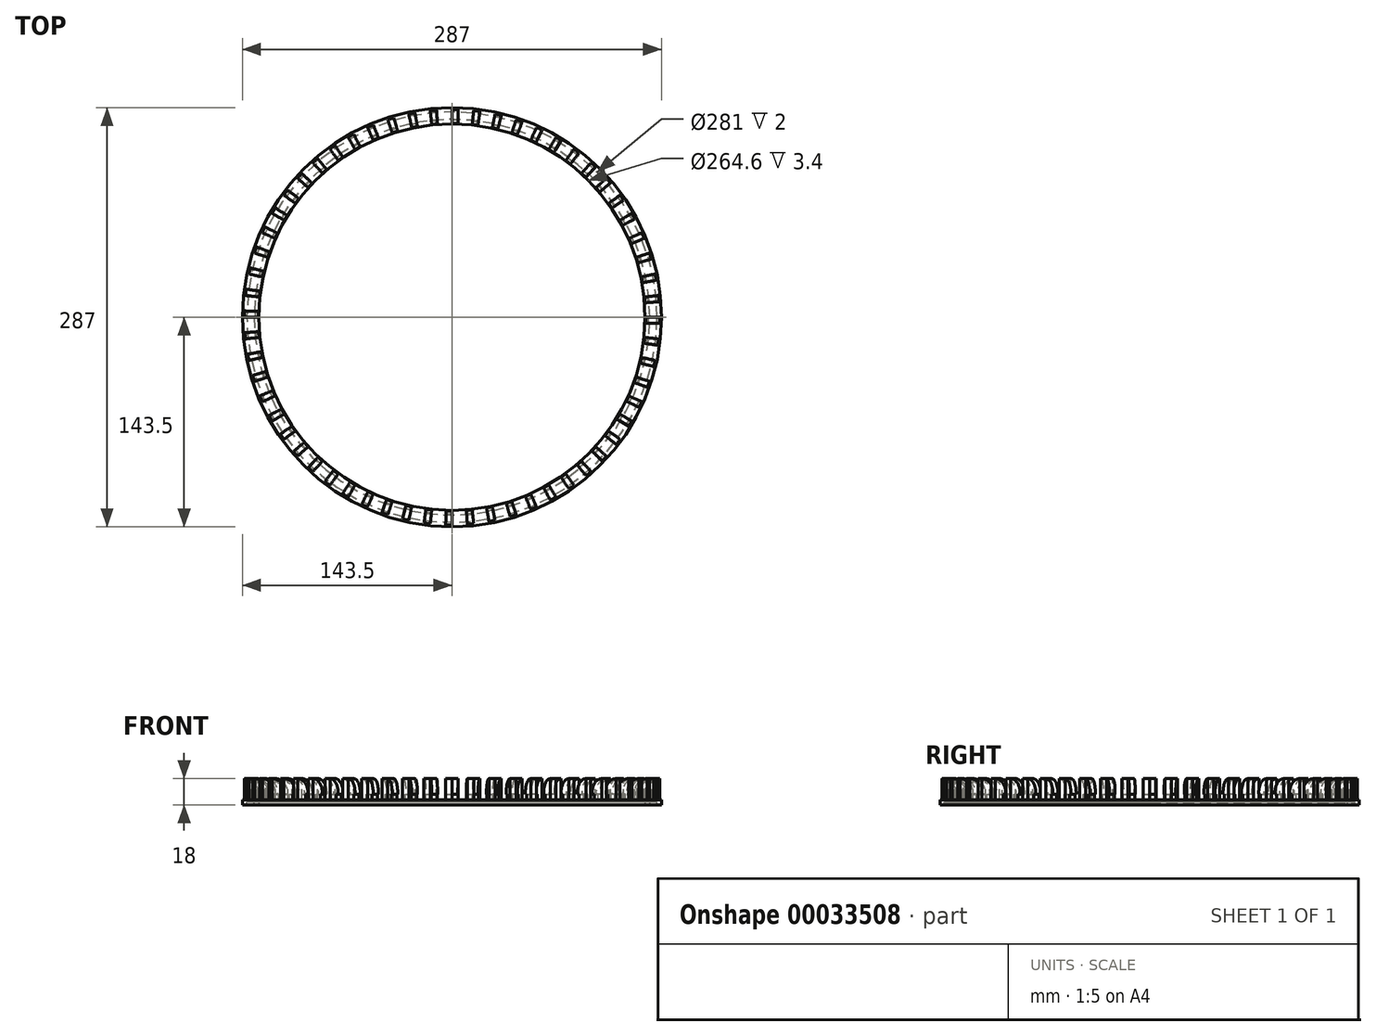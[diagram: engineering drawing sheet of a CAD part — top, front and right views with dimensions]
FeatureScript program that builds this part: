
annotation { "Feature Type Name" : "Feature", "Feature Type Description" : "" }
export const myFeature = defineFeature(function(context is Context, id is Id, definition is map)
    precondition{}
    {
        {
            var Q0;
            Q0=qCreatedBy(makeId("Top.planeOp"),FACE);
            var sketch = newSketch(context, id + "F0", { "sketchPlane" : qUnion([Q0])});
            skCircle(sketch, "E0", {"center": v(0, 0) * mm, "radius": 132.3 * mm});
            skCircle(sketch, "E1", {"center": v(0, 0) * mm, "radius": 143.5 * mm});
            skSolve(sketch);
        }
        {
            var Q0;
            Q0=makeQuery(id+"F0.imprint","IMPRINT",FACE,{"disambiguationData":[TD([[makeQuery(id+"F0.imprint","IMPRINT",EDGE,{"derivedFrom":sQuery(id+"F0.wireOp",EDGE,"E0")}),-1.0]])]});
            extrude(context, id + "F1", {"entities" : qUnion([Q0]), "depth" : 18 * mm});
        }
        {
            var Q0;
            Q0=qCreatedBy(makeId("Front.planeOp"),FACE);
            var sketch = newSketch(context, id + "F2", { "sketchPlane" : qUnion([Q0])});
            skLineSegment(sketch, "E2.rect.bottom", {"start": v(-132.3, 0) * mm, "end": v(-143.5, 0) * mm, "construction": true});
            skLineSegment(sketch, "E2.rect.top", {"start": v(-132.3, 18) * mm, "end": v(-143.5, 18) * mm, "construction": true});
            skLineSegment(sketch, "E2.rect.left", {"start": v(-132.3, 0) * mm, "end": v(-132.3, 18) * mm, "construction": true});
            skLineSegment(sketch, "E2.rect.right", {"start": v(-143.5, 0) * mm, "end": v(-143.5, 18) * mm, "construction": true});
            skPoint(sketch, "E2.rect.middle", {"position": v(-137.9, 9) * mm});
            skLineSegment(sketch, "E3", {"start": v(-143.5, 3.4) * mm, "end": v(-142.2, 3.4) * mm});
            skLineSegment(sketch, "E4", {"start": v(-142.2, 3.4) * mm, "end": v(-142.2, 18) * mm});
            skLineSegment(sketch, "E5", {"start": v(-132.3, 3.4) * mm, "end": v(-134.8, 3.4) * mm});
            skLineSegment(sketch, "E6", {"start": v(-134.8, 3.4) * mm, "end": v(-134.8, 7.4) * mm});
            skLineSegment(sketch, "E7", {"start": v(-134.8, 7.4) * mm, "end": v(-132.8, 7.4) * mm});
            skArc(sketch, "E8", {"start": v(-132.8, 7.4) * mm, "mid": v(-135.12, 14.81) * mm, "end": v(-142.2, 18) * mm});
            skLineSegment(sketch, "E9", {"start": v(-142.2, 18) * mm, "end": v(-142.2, -0.94) * mm, "construction": true});
            skLineSegment(sketch, "E10", {"start": v(-132.3, 3.4) * mm, "end": v(-132.3, 18) * mm});
            skLineSegment(sketch, "E11", {"start": v(-143.5, 18) * mm, "end": v(-143.5, 3.4) * mm});
            skLineSegment(sketch, "E12", {"start": v(-142.2, 18) * mm, "end": v(-132.3, 18) * mm});
            skLineSegment(sketch, "E13", {"start": v(-142.2, 18) * mm, "end": v(-143.5, 18) * mm});
            skLineSegment(sketch, "E14", {"start": v(0, 0) * mm, "end": v(0, 83.23) * mm, "construction": true});
            skLineSegment(sketch, "E15.bottom", {"start": v(-140.5, 0) * mm, "end": v(-135.5, 0) * mm});
            skLineSegment(sketch, "E15.top", {"start": v(-140.5, 2) * mm, "end": v(-135.5, 2) * mm});
            skLineSegment(sketch, "E15.left", {"start": v(-140.5, 0) * mm, "end": v(-140.5, 2) * mm});
            skLineSegment(sketch, "E15.right", {"start": v(-135.5, 0) * mm, "end": v(-135.5, 2) * mm});
            skSolve(sketch);
        }
        {
            var Q0;
            Q0 = qSketchRegion(id + "F2", true);
            var Q1;
            Q1=sQuery(id+"F2.wireOp",EDGE,"E14");
            revolve(context, id + "F3", {"operationType" : NewBodyOperationType.REMOVE, "entities" : qUnion([Q0]), "axis" : qUnion([Q1]), "revolveType" : RevolveType.FULL, "oppositeDirection" : true});
        }
        {
            var Q0;
            Q0=makeQuery(id+"F3.boolean.opBoolean","COPY",FACE,{"derivedFrom":makeQuery(id+"F3.opRevolve","SWEPT_FACE",FACE,{"disambiguationData":[OSD([sQuery(id+"F2.wireOp",EDGE,"E3")])]})});
            var sketch = newSketch(context, id + "F4", { "sketchPlane" : qUnion([Q0])});
            skLineSegment(sketch, "E16", {"start": v(0, 0) * mm, "end": v(-143.5, 0) * mm, "construction": true});
            skLineSegment(sketch, "E17", {"start": v(0, 0) * mm, "end": v(-142.71, 15) * mm, "construction": true});
            skLineSegment(sketch, "E18.bottom", {"start": v(-143.5, 0) * mm, "end": v(-132.3, 0) * mm, "construction": true});
            skLineSegment(sketch, "E18.top", {"start": v(-143.5, 4) * mm, "end": v(-132.3, 4) * mm, "construction": true});
            skLineSegment(sketch, "E18.left", {"start": v(-143.5, 0) * mm, "end": v(-143.5, 4) * mm, "construction": true});
            skLineSegment(sketch, "E18.right", {"start": v(-132.3, 0) * mm, "end": v(-132.3, 4) * mm, "construction": true});
            skLineSegment(sketch, "E19", {"start": v(0, 0) * mm, "end": v(-143.43, 4.34) * mm, "construction": true});
            skLineSegment(sketch, "E20", {"start": v(-142.71, 15) * mm, "end": v(-131.58, 13.83) * mm});
            skLineSegment(sketch, "E21", {"start": v(-143.43, 4.34) * mm, "end": v(-132.24, 4) * mm});
            skArc(sketch, "E22", {"start": v(-142.71, 15) * mm, "mid": v(-143.17, 9.67) * mm, "end": v(-143.43, 4.34) * mm});
            skArc(sketch, "E23", {"start": v(-131.58, 13.83) * mm, "mid": v(-132, 8.92) * mm, "end": v(-132.24, 4) * mm});
            skArc(sketch, "E24.1.0", {"start": v(-143.5, 0) * mm, "mid": v(-143.4, -5.34) * mm, "end": v(-143.1, -10.68) * mm});
            skLineSegment(sketch, "E24.1.1", {"start": v(-143.1, -10.68) * mm, "end": v(-131.93, -9.85) * mm});
            skLineSegment(sketch, "E24.1.2", {"start": v(-143.5, 0) * mm, "end": v(-132.3, 0) * mm});
            skArc(sketch, "E24.1.3", {"start": v(-132.3, 0) * mm, "mid": v(-132.2, -4.93) * mm, "end": v(-131.93, -9.85) * mm});
            skArc(sketch, "E24.2.0", {"start": v(-142.71, -15) * mm, "mid": v(-142.06, -20.3) * mm, "end": v(-141.2, -25.58) * mm});
            skLineSegment(sketch, "E24.2.1", {"start": v(-141.2, -25.58) * mm, "end": v(-130.18, -23.58) * mm});
            skLineSegment(sketch, "E24.2.2", {"start": v(-142.71, -15) * mm, "end": v(-131.58, -13.83) * mm});
            skArc(sketch, "E24.2.3", {"start": v(-131.58, -13.83) * mm, "mid": v(-130.97, -18.72) * mm, "end": v(-130.18, -23.58) * mm});
            skArc(sketch, "E24.3.0", {"start": v(-140.36, -29.84) * mm, "mid": v(-139.16, -35.04) * mm, "end": v(-137.75, -40.2) * mm});
            skLineSegment(sketch, "E24.3.1", {"start": v(-137.75, -40.2) * mm, "end": v(-127, -37.06) * mm});
            skLineSegment(sketch, "E24.3.2", {"start": v(-140.36, -29.84) * mm, "end": v(-129.4, -27.5) * mm});
            skArc(sketch, "E24.3.3", {"start": v(-129.4, -27.5) * mm, "mid": v(-128.3, -32.3) * mm, "end": v(-127, -37.06) * mm});
            skArc(sketch, "E24.4.0", {"start": v(-136.48, -44.34) * mm, "mid": v(-134.73, -49.4) * mm, "end": v(-132.8, -54.38) * mm});
            skLineSegment(sketch, "E24.4.1", {"start": v(-132.8, -54.38) * mm, "end": v(-122.43, -50.13) * mm});
            skLineSegment(sketch, "E24.4.2", {"start": v(-136.48, -44.34) * mm, "end": v(-125.82, -40.88) * mm});
            skArc(sketch, "E24.4.3", {"start": v(-125.82, -40.88) * mm, "mid": v(-124.22, -45.54) * mm, "end": v(-122.43, -50.13) * mm});
            skArc(sketch, "E24.5.0", {"start": v(-131.1, -58.37) * mm, "mid": v(-128.83, -63.2) * mm, "end": v(-126.39, -67.96) * mm});
            skLineSegment(sketch, "E24.5.1", {"start": v(-126.39, -67.96) * mm, "end": v(-116.52, -62.66) * mm});
            skLineSegment(sketch, "E24.5.2", {"start": v(-131.1, -58.37) * mm, "end": v(-120.86, -53.81) * mm});
            skArc(sketch, "E24.5.3", {"start": v(-120.86, -53.81) * mm, "mid": v(-118.77, -58.27) * mm, "end": v(-116.52, -62.66) * mm});
            skArc(sketch, "E24.6.0", {"start": v(-124.27, -71.75) * mm, "mid": v(-121.52, -76.33) * mm, "end": v(-118.59, -80.8) * mm});
            skLineSegment(sketch, "E24.6.1", {"start": v(-118.59, -80.8) * mm, "end": v(-109.33, -74.5) * mm});
            skLineSegment(sketch, "E24.6.2", {"start": v(-124.27, -71.75) * mm, "end": v(-114.58, -66.15) * mm});
            skArc(sketch, "E24.6.3", {"start": v(-114.58, -66.15) * mm, "mid": v(-112.03, -70.37) * mm, "end": v(-109.33, -74.5) * mm});
            skArc(sketch, "E24.7.0", {"start": v(-116.1, -84.35) * mm, "mid": v(-112.87, -88.61) * mm, "end": v(-109.5, -92.75) * mm});
            skLineSegment(sketch, "E24.7.1", {"start": v(-109.5, -92.75) * mm, "end": v(-100.95, -85.51) * mm});
            skLineSegment(sketch, "E24.7.2", {"start": v(-116.1, -84.35) * mm, "end": v(-107.03, -77.76) * mm});
            skArc(sketch, "E24.7.3", {"start": v(-107.03, -77.76) * mm, "mid": v(-104.06, -81.7) * mm, "end": v(-100.95, -85.51) * mm});
            skArc(sketch, "E24.8.0", {"start": v(-106.64, -96.02) * mm, "mid": v(-103, -99.92) * mm, "end": v(-99.2, -103.7) * mm});
            skLineSegment(sketch, "E24.8.1", {"start": v(-99.2, -103.7) * mm, "end": v(-91.46, -95.6) * mm});
            skLineSegment(sketch, "E24.8.2", {"start": v(-106.64, -96.02) * mm, "end": v(-98.32, -88.53) * mm});
            skArc(sketch, "E24.8.3", {"start": v(-98.32, -88.53) * mm, "mid": v(-94.95, -92.13) * mm, "end": v(-91.46, -95.6) * mm});
            skArc(sketch, "E24.9.0", {"start": v(-96.02, -106.64) * mm, "mid": v(-91.98, -110.14) * mm, "end": v(-87.82, -113.5) * mm});
            skLineSegment(sketch, "E24.9.1", {"start": v(-87.82, -113.5) * mm, "end": v(-80.96, -104.63) * mm});
            skLineSegment(sketch, "E24.9.2", {"start": v(-96.02, -106.64) * mm, "end": v(-88.53, -98.32) * mm});
            skArc(sketch, "E24.9.3", {"start": v(-88.53, -98.32) * mm, "mid": v(-84.8, -101.55) * mm, "end": v(-80.96, -104.63) * mm});
            skArc(sketch, "E24.10.0", {"start": v(-84.35, -116.1) * mm, "mid": v(-79.97, -119.15) * mm, "end": v(-75.47, -122.05) * mm});
            skLineSegment(sketch, "E24.10.1", {"start": v(-75.47, -122.05) * mm, "end": v(-69.58, -112.52) * mm});
            skLineSegment(sketch, "E24.10.2", {"start": v(-84.35, -116.1) * mm, "end": v(-77.76, -107.03) * mm});
            skArc(sketch, "E24.10.3", {"start": v(-77.76, -107.03) * mm, "mid": v(-73.72, -109.85) * mm, "end": v(-69.58, -112.52) * mm});
            skArc(sketch, "E24.11.0", {"start": v(-71.75, -124.27) * mm, "mid": v(-67.07, -126.86) * mm, "end": v(-62.3, -129.27) * mm});
            skLineSegment(sketch, "E24.11.1", {"start": v(-62.3, -129.27) * mm, "end": v(-57.44, -119.18) * mm});
            skLineSegment(sketch, "E24.11.2", {"start": v(-71.75, -124.27) * mm, "end": v(-66.15, -114.58) * mm});
            skArc(sketch, "E24.11.3", {"start": v(-66.15, -114.58) * mm, "mid": v(-61.84, -116.96) * mm, "end": v(-57.44, -119.18) * mm});
            skArc(sketch, "E24.12.0", {"start": v(-58.37, -131.1) * mm, "mid": v(-53.44, -133.18) * mm, "end": v(-48.45, -135.07) * mm});
            skLineSegment(sketch, "E24.12.1", {"start": v(-48.45, -135.07) * mm, "end": v(-44.67, -124.53) * mm});
            skLineSegment(sketch, "E24.12.2", {"start": v(-58.37, -131.1) * mm, "end": v(-53.81, -120.86) * mm});
            skArc(sketch, "E24.12.3", {"start": v(-53.81, -120.86) * mm, "mid": v(-49.27, -122.78) * mm, "end": v(-44.67, -124.53) * mm});
            skArc(sketch, "E24.13.0", {"start": v(-44.34, -136.48) * mm, "mid": v(-39.23, -138.03) * mm, "end": v(-34.06, -139.4) * mm});
            skLineSegment(sketch, "E24.13.1", {"start": v(-34.06, -139.4) * mm, "end": v(-31.4, -128.52) * mm});
            skLineSegment(sketch, "E24.13.2", {"start": v(-44.34, -136.48) * mm, "end": v(-40.88, -125.82) * mm});
            skArc(sketch, "E24.13.3", {"start": v(-40.88, -125.82) * mm, "mid": v(-36.17, -127.26) * mm, "end": v(-31.4, -128.52) * mm});
            skArc(sketch, "E24.14.0", {"start": v(-29.84, -140.36) * mm, "mid": v(-24.59, -141.38) * mm, "end": v(-19.3, -142.2) * mm});
            skLineSegment(sketch, "E24.14.1", {"start": v(-19.3, -142.2) * mm, "end": v(-17.8, -131.1) * mm});
            skLineSegment(sketch, "E24.14.2", {"start": v(-29.84, -140.36) * mm, "end": v(-27.5, -129.4) * mm});
            skArc(sketch, "E24.14.3", {"start": v(-27.5, -129.4) * mm, "mid": v(-22.67, -130.34) * mm, "end": v(-17.8, -131.1) * mm});
            skArc(sketch, "E24.15.0", {"start": v(-15, -142.71) * mm, "mid": v(-9.67, -143.17) * mm, "end": v(-4.34, -143.43) * mm});
            skLineSegment(sketch, "E24.15.1", {"start": v(-4.34, -143.43) * mm, "end": v(-4, -132.24) * mm});
            skLineSegment(sketch, "E24.15.2", {"start": v(-15, -142.71) * mm, "end": v(-13.83, -131.58) * mm});
            skArc(sketch, "E24.15.3", {"start": v(-13.83, -131.58) * mm, "mid": v(-8.92, -132) * mm, "end": v(-4, -132.24) * mm});
            skArc(sketch, "E24.16.0", {"start": v(0, -143.5) * mm, "mid": v(5.34, -143.4) * mm, "end": v(10.68, -143.1) * mm});
            skLineSegment(sketch, "E24.16.1", {"start": v(10.68, -143.1) * mm, "end": v(9.85, -131.93) * mm});
            skLineSegment(sketch, "E24.16.2", {"start": v(0, -143.5) * mm, "end": v(0, -132.3) * mm});
            skArc(sketch, "E24.16.3", {"start": v(0, -132.3) * mm, "mid": v(4.93, -132.2) * mm, "end": v(9.85, -131.93) * mm});
            skArc(sketch, "E24.17.0", {"start": v(15, -142.71) * mm, "mid": v(20.3, -142.06) * mm, "end": v(25.58, -141.2) * mm});
            skLineSegment(sketch, "E24.17.1", {"start": v(25.58, -141.2) * mm, "end": v(23.58, -130.18) * mm});
            skLineSegment(sketch, "E24.17.2", {"start": v(15, -142.71) * mm, "end": v(13.83, -131.58) * mm});
            skArc(sketch, "E24.17.3", {"start": v(13.83, -131.58) * mm, "mid": v(18.72, -130.97) * mm, "end": v(23.58, -130.18) * mm});
            skArc(sketch, "E24.18.0", {"start": v(29.84, -140.36) * mm, "mid": v(35.04, -139.16) * mm, "end": v(40.2, -137.75) * mm});
            skLineSegment(sketch, "E24.18.1", {"start": v(40.2, -137.75) * mm, "end": v(37.06, -127) * mm});
            skLineSegment(sketch, "E24.18.2", {"start": v(29.84, -140.36) * mm, "end": v(27.5, -129.4) * mm});
            skArc(sketch, "E24.18.3", {"start": v(27.5, -129.4) * mm, "mid": v(32.3, -128.3) * mm, "end": v(37.06, -127) * mm});
            skArc(sketch, "E24.19.0", {"start": v(44.34, -136.48) * mm, "mid": v(49.4, -134.73) * mm, "end": v(54.38, -132.8) * mm});
            skLineSegment(sketch, "E24.19.1", {"start": v(54.38, -132.8) * mm, "end": v(50.13, -122.43) * mm});
            skLineSegment(sketch, "E24.19.2", {"start": v(44.34, -136.48) * mm, "end": v(40.88, -125.82) * mm});
            skArc(sketch, "E24.19.3", {"start": v(40.88, -125.82) * mm, "mid": v(45.54, -124.22) * mm, "end": v(50.13, -122.43) * mm});
            skArc(sketch, "E24.20.0", {"start": v(58.37, -131.1) * mm, "mid": v(63.2, -128.83) * mm, "end": v(67.96, -126.39) * mm});
            skLineSegment(sketch, "E24.20.1", {"start": v(67.96, -126.39) * mm, "end": v(62.66, -116.52) * mm});
            skLineSegment(sketch, "E24.20.2", {"start": v(58.37, -131.1) * mm, "end": v(53.81, -120.86) * mm});
            skArc(sketch, "E24.20.3", {"start": v(53.81, -120.86) * mm, "mid": v(58.27, -118.77) * mm, "end": v(62.66, -116.52) * mm});
            skArc(sketch, "E24.21.0", {"start": v(71.75, -124.27) * mm, "mid": v(76.33, -121.52) * mm, "end": v(80.8, -118.59) * mm});
            skLineSegment(sketch, "E24.21.1", {"start": v(80.8, -118.59) * mm, "end": v(74.5, -109.33) * mm});
            skLineSegment(sketch, "E24.21.2", {"start": v(71.75, -124.27) * mm, "end": v(66.15, -114.58) * mm});
            skArc(sketch, "E24.21.3", {"start": v(66.15, -114.58) * mm, "mid": v(70.37, -112.03) * mm, "end": v(74.5, -109.33) * mm});
            skArc(sketch, "E24.22.0", {"start": v(84.35, -116.1) * mm, "mid": v(88.61, -112.87) * mm, "end": v(92.75, -109.5) * mm});
            skLineSegment(sketch, "E24.22.1", {"start": v(92.75, -109.5) * mm, "end": v(85.51, -100.95) * mm});
            skLineSegment(sketch, "E24.22.2", {"start": v(84.35, -116.1) * mm, "end": v(77.76, -107.03) * mm});
            skArc(sketch, "E24.22.3", {"start": v(77.76, -107.03) * mm, "mid": v(81.7, -104.06) * mm, "end": v(85.51, -100.95) * mm});
            skArc(sketch, "E24.23.0", {"start": v(96.02, -106.64) * mm, "mid": v(99.92, -103) * mm, "end": v(103.7, -99.2) * mm});
            skLineSegment(sketch, "E24.23.1", {"start": v(103.7, -99.2) * mm, "end": v(95.6, -91.46) * mm});
            skLineSegment(sketch, "E24.23.2", {"start": v(96.02, -106.64) * mm, "end": v(88.53, -98.32) * mm});
            skArc(sketch, "E24.23.3", {"start": v(88.53, -98.32) * mm, "mid": v(92.13, -94.95) * mm, "end": v(95.6, -91.46) * mm});
            skArc(sketch, "E24.24.0", {"start": v(106.64, -96.02) * mm, "mid": v(110.14, -91.98) * mm, "end": v(113.5, -87.82) * mm});
            skLineSegment(sketch, "E24.24.1", {"start": v(113.5, -87.82) * mm, "end": v(104.63, -80.96) * mm});
            skLineSegment(sketch, "E24.24.2", {"start": v(106.64, -96.02) * mm, "end": v(98.32, -88.53) * mm});
            skArc(sketch, "E24.24.3", {"start": v(98.32, -88.53) * mm, "mid": v(101.55, -84.8) * mm, "end": v(104.63, -80.96) * mm});
            skArc(sketch, "E24.25.0", {"start": v(116.1, -84.35) * mm, "mid": v(119.15, -79.97) * mm, "end": v(122.05, -75.47) * mm});
            skLineSegment(sketch, "E24.25.1", {"start": v(122.05, -75.47) * mm, "end": v(112.52, -69.58) * mm});
            skLineSegment(sketch, "E24.25.2", {"start": v(116.1, -84.35) * mm, "end": v(107.03, -77.76) * mm});
            skArc(sketch, "E24.25.3", {"start": v(107.03, -77.76) * mm, "mid": v(109.85, -73.72) * mm, "end": v(112.52, -69.58) * mm});
            skArc(sketch, "E24.26.0", {"start": v(124.27, -71.75) * mm, "mid": v(126.86, -67.07) * mm, "end": v(129.27, -62.3) * mm});
            skLineSegment(sketch, "E24.26.1", {"start": v(129.27, -62.3) * mm, "end": v(119.18, -57.44) * mm});
            skLineSegment(sketch, "E24.26.2", {"start": v(124.27, -71.75) * mm, "end": v(114.58, -66.15) * mm});
            skArc(sketch, "E24.26.3", {"start": v(114.58, -66.15) * mm, "mid": v(116.96, -61.84) * mm, "end": v(119.18, -57.44) * mm});
            skArc(sketch, "E24.27.0", {"start": v(131.1, -58.37) * mm, "mid": v(133.18, -53.44) * mm, "end": v(135.07, -48.45) * mm});
            skLineSegment(sketch, "E24.27.1", {"start": v(135.07, -48.45) * mm, "end": v(124.53, -44.67) * mm});
            skLineSegment(sketch, "E24.27.2", {"start": v(131.1, -58.37) * mm, "end": v(120.86, -53.81) * mm});
            skArc(sketch, "E24.27.3", {"start": v(120.86, -53.81) * mm, "mid": v(122.78, -49.27) * mm, "end": v(124.53, -44.67) * mm});
            skArc(sketch, "E24.28.0", {"start": v(136.48, -44.34) * mm, "mid": v(138.03, -39.23) * mm, "end": v(139.4, -34.06) * mm});
            skLineSegment(sketch, "E24.28.1", {"start": v(139.4, -34.06) * mm, "end": v(128.52, -31.4) * mm});
            skLineSegment(sketch, "E24.28.2", {"start": v(136.48, -44.34) * mm, "end": v(125.82, -40.88) * mm});
            skArc(sketch, "E24.28.3", {"start": v(125.82, -40.88) * mm, "mid": v(127.26, -36.17) * mm, "end": v(128.52, -31.4) * mm});
            skArc(sketch, "E24.29.0", {"start": v(140.36, -29.84) * mm, "mid": v(141.38, -24.59) * mm, "end": v(142.2, -19.3) * mm});
            skLineSegment(sketch, "E24.29.1", {"start": v(142.2, -19.3) * mm, "end": v(131.1, -17.8) * mm});
            skLineSegment(sketch, "E24.29.2", {"start": v(140.36, -29.84) * mm, "end": v(129.4, -27.5) * mm});
            skArc(sketch, "E24.29.3", {"start": v(129.4, -27.5) * mm, "mid": v(130.34, -22.67) * mm, "end": v(131.1, -17.8) * mm});
            skArc(sketch, "E24.30.0", {"start": v(142.71, -15) * mm, "mid": v(143.17, -9.67) * mm, "end": v(143.43, -4.34) * mm});
            skLineSegment(sketch, "E24.30.1", {"start": v(143.43, -4.34) * mm, "end": v(132.24, -4) * mm});
            skLineSegment(sketch, "E24.30.2", {"start": v(142.71, -15) * mm, "end": v(131.58, -13.83) * mm});
            skArc(sketch, "E24.30.3", {"start": v(131.58, -13.83) * mm, "mid": v(132, -8.92) * mm, "end": v(132.24, -4) * mm});
            skArc(sketch, "E24.31.0", {"start": v(143.5, 0) * mm, "mid": v(143.4, 5.34) * mm, "end": v(143.1, 10.68) * mm});
            skLineSegment(sketch, "E24.31.1", {"start": v(143.1, 10.68) * mm, "end": v(131.93, 9.85) * mm});
            skLineSegment(sketch, "E24.31.2", {"start": v(143.5, 0) * mm, "end": v(132.3, 0) * mm});
            skArc(sketch, "E24.31.3", {"start": v(132.3, 0) * mm, "mid": v(132.2, 4.93) * mm, "end": v(131.93, 9.85) * mm});
            skArc(sketch, "E24.32.0", {"start": v(142.71, 15) * mm, "mid": v(142.06, 20.3) * mm, "end": v(141.2, 25.58) * mm});
            skLineSegment(sketch, "E24.32.1", {"start": v(141.2, 25.58) * mm, "end": v(130.18, 23.58) * mm});
            skLineSegment(sketch, "E24.32.2", {"start": v(142.71, 15) * mm, "end": v(131.58, 13.83) * mm});
            skArc(sketch, "E24.32.3", {"start": v(131.58, 13.83) * mm, "mid": v(130.97, 18.72) * mm, "end": v(130.18, 23.58) * mm});
            skArc(sketch, "E24.33.0", {"start": v(140.36, 29.84) * mm, "mid": v(139.16, 35.04) * mm, "end": v(137.75, 40.2) * mm});
            skLineSegment(sketch, "E24.33.1", {"start": v(137.75, 40.2) * mm, "end": v(127, 37.06) * mm});
            skLineSegment(sketch, "E24.33.2", {"start": v(140.36, 29.84) * mm, "end": v(129.4, 27.5) * mm});
            skArc(sketch, "E24.33.3", {"start": v(129.4, 27.5) * mm, "mid": v(128.3, 32.3) * mm, "end": v(127, 37.06) * mm});
            skArc(sketch, "E24.34.0", {"start": v(136.48, 44.34) * mm, "mid": v(134.73, 49.4) * mm, "end": v(132.8, 54.38) * mm});
            skLineSegment(sketch, "E24.34.1", {"start": v(132.8, 54.38) * mm, "end": v(122.43, 50.13) * mm});
            skLineSegment(sketch, "E24.34.2", {"start": v(136.48, 44.34) * mm, "end": v(125.82, 40.88) * mm});
            skArc(sketch, "E24.34.3", {"start": v(125.82, 40.88) * mm, "mid": v(124.22, 45.54) * mm, "end": v(122.43, 50.13) * mm});
            skArc(sketch, "E24.35.0", {"start": v(131.1, 58.37) * mm, "mid": v(128.83, 63.2) * mm, "end": v(126.39, 67.96) * mm});
            skLineSegment(sketch, "E24.35.1", {"start": v(126.39, 67.96) * mm, "end": v(116.52, 62.66) * mm});
            skLineSegment(sketch, "E24.35.2", {"start": v(131.1, 58.37) * mm, "end": v(120.86, 53.81) * mm});
            skArc(sketch, "E24.35.3", {"start": v(120.86, 53.81) * mm, "mid": v(118.77, 58.27) * mm, "end": v(116.52, 62.66) * mm});
            skArc(sketch, "E24.36.0", {"start": v(124.27, 71.75) * mm, "mid": v(121.52, 76.33) * mm, "end": v(118.59, 80.8) * mm});
            skLineSegment(sketch, "E24.36.1", {"start": v(118.59, 80.8) * mm, "end": v(109.33, 74.5) * mm});
            skLineSegment(sketch, "E24.36.2", {"start": v(124.27, 71.75) * mm, "end": v(114.58, 66.15) * mm});
            skArc(sketch, "E24.36.3", {"start": v(114.58, 66.15) * mm, "mid": v(112.03, 70.37) * mm, "end": v(109.33, 74.5) * mm});
            skArc(sketch, "E24.37.0", {"start": v(116.1, 84.35) * mm, "mid": v(112.87, 88.61) * mm, "end": v(109.5, 92.75) * mm});
            skLineSegment(sketch, "E24.37.1", {"start": v(109.5, 92.75) * mm, "end": v(100.95, 85.51) * mm});
            skLineSegment(sketch, "E24.37.2", {"start": v(116.1, 84.35) * mm, "end": v(107.03, 77.76) * mm});
            skArc(sketch, "E24.37.3", {"start": v(107.03, 77.76) * mm, "mid": v(104.06, 81.7) * mm, "end": v(100.95, 85.51) * mm});
            skArc(sketch, "E24.38.0", {"start": v(106.64, 96.02) * mm, "mid": v(103, 99.92) * mm, "end": v(99.2, 103.7) * mm});
            skLineSegment(sketch, "E24.38.1", {"start": v(99.2, 103.7) * mm, "end": v(91.46, 95.6) * mm});
            skLineSegment(sketch, "E24.38.2", {"start": v(106.64, 96.02) * mm, "end": v(98.32, 88.53) * mm});
            skArc(sketch, "E24.38.3", {"start": v(98.32, 88.53) * mm, "mid": v(94.95, 92.13) * mm, "end": v(91.46, 95.6) * mm});
            skArc(sketch, "E24.39.0", {"start": v(96.02, 106.64) * mm, "mid": v(91.98, 110.14) * mm, "end": v(87.82, 113.5) * mm});
            skLineSegment(sketch, "E24.39.1", {"start": v(87.82, 113.5) * mm, "end": v(80.96, 104.63) * mm});
            skLineSegment(sketch, "E24.39.2", {"start": v(96.02, 106.64) * mm, "end": v(88.53, 98.32) * mm});
            skArc(sketch, "E24.39.3", {"start": v(88.53, 98.32) * mm, "mid": v(84.8, 101.55) * mm, "end": v(80.96, 104.63) * mm});
            skArc(sketch, "E24.40.0", {"start": v(84.35, 116.1) * mm, "mid": v(79.97, 119.15) * mm, "end": v(75.47, 122.05) * mm});
            skLineSegment(sketch, "E24.40.1", {"start": v(75.47, 122.05) * mm, "end": v(69.58, 112.52) * mm});
            skLineSegment(sketch, "E24.40.2", {"start": v(84.35, 116.1) * mm, "end": v(77.76, 107.03) * mm});
            skArc(sketch, "E24.40.3", {"start": v(77.76, 107.03) * mm, "mid": v(73.72, 109.85) * mm, "end": v(69.58, 112.52) * mm});
            skArc(sketch, "E24.41.0", {"start": v(71.75, 124.27) * mm, "mid": v(67.07, 126.86) * mm, "end": v(62.3, 129.27) * mm});
            skLineSegment(sketch, "E24.41.1", {"start": v(62.3, 129.27) * mm, "end": v(57.44, 119.18) * mm});
            skLineSegment(sketch, "E24.41.2", {"start": v(71.75, 124.27) * mm, "end": v(66.15, 114.58) * mm});
            skArc(sketch, "E24.41.3", {"start": v(66.15, 114.58) * mm, "mid": v(61.84, 116.96) * mm, "end": v(57.44, 119.18) * mm});
            skArc(sketch, "E24.42.0", {"start": v(58.37, 131.1) * mm, "mid": v(53.44, 133.18) * mm, "end": v(48.45, 135.07) * mm});
            skLineSegment(sketch, "E24.42.1", {"start": v(48.45, 135.07) * mm, "end": v(44.67, 124.53) * mm});
            skLineSegment(sketch, "E24.42.2", {"start": v(58.37, 131.1) * mm, "end": v(53.81, 120.86) * mm});
            skArc(sketch, "E24.42.3", {"start": v(53.81, 120.86) * mm, "mid": v(49.27, 122.78) * mm, "end": v(44.67, 124.53) * mm});
            skArc(sketch, "E24.43.0", {"start": v(44.34, 136.48) * mm, "mid": v(39.23, 138.03) * mm, "end": v(34.06, 139.4) * mm});
            skLineSegment(sketch, "E24.43.1", {"start": v(34.06, 139.4) * mm, "end": v(31.4, 128.52) * mm});
            skLineSegment(sketch, "E24.43.2", {"start": v(44.34, 136.48) * mm, "end": v(40.88, 125.82) * mm});
            skArc(sketch, "E24.43.3", {"start": v(40.88, 125.82) * mm, "mid": v(36.17, 127.26) * mm, "end": v(31.4, 128.52) * mm});
            skArc(sketch, "E24.44.0", {"start": v(29.84, 140.36) * mm, "mid": v(24.59, 141.38) * mm, "end": v(19.3, 142.2) * mm});
            skLineSegment(sketch, "E24.44.1", {"start": v(19.3, 142.2) * mm, "end": v(17.8, 131.1) * mm});
            skLineSegment(sketch, "E24.44.2", {"start": v(29.84, 140.36) * mm, "end": v(27.5, 129.4) * mm});
            skArc(sketch, "E24.44.3", {"start": v(27.5, 129.4) * mm, "mid": v(22.67, 130.34) * mm, "end": v(17.8, 131.1) * mm});
            skArc(sketch, "E24.45.0", {"start": v(15, 142.71) * mm, "mid": v(9.67, 143.17) * mm, "end": v(4.34, 143.43) * mm});
            skLineSegment(sketch, "E24.45.1", {"start": v(4.34, 143.43) * mm, "end": v(4, 132.24) * mm});
            skLineSegment(sketch, "E24.45.2", {"start": v(15, 142.71) * mm, "end": v(13.83, 131.58) * mm});
            skArc(sketch, "E24.45.3", {"start": v(13.83, 131.58) * mm, "mid": v(8.92, 132) * mm, "end": v(4, 132.24) * mm});
            skArc(sketch, "E24.46.0", {"start": v(0, 143.5) * mm, "mid": v(-5.34, 143.4) * mm, "end": v(-10.68, 143.1) * mm});
            skLineSegment(sketch, "E24.46.1", {"start": v(-10.68, 143.1) * mm, "end": v(-9.85, 131.93) * mm});
            skLineSegment(sketch, "E24.46.2", {"start": v(0, 143.5) * mm, "end": v(0, 132.3) * mm});
            skArc(sketch, "E24.46.3", {"start": v(0, 132.3) * mm, "mid": v(-4.93, 132.2) * mm, "end": v(-9.85, 131.93) * mm});
            skArc(sketch, "E24.47.0", {"start": v(-15, 142.71) * mm, "mid": v(-20.3, 142.06) * mm, "end": v(-25.58, 141.2) * mm});
            skLineSegment(sketch, "E24.47.1", {"start": v(-25.58, 141.2) * mm, "end": v(-23.58, 130.18) * mm});
            skLineSegment(sketch, "E24.47.2", {"start": v(-15, 142.71) * mm, "end": v(-13.83, 131.58) * mm});
            skArc(sketch, "E24.47.3", {"start": v(-13.83, 131.58) * mm, "mid": v(-18.72, 130.97) * mm, "end": v(-23.58, 130.18) * mm});
            skArc(sketch, "E24.48.0", {"start": v(-29.84, 140.36) * mm, "mid": v(-35.04, 139.16) * mm, "end": v(-40.2, 137.75) * mm});
            skLineSegment(sketch, "E24.48.1", {"start": v(-40.2, 137.75) * mm, "end": v(-37.06, 127) * mm});
            skLineSegment(sketch, "E24.48.2", {"start": v(-29.84, 140.36) * mm, "end": v(-27.5, 129.4) * mm});
            skArc(sketch, "E24.48.3", {"start": v(-27.5, 129.4) * mm, "mid": v(-32.3, 128.3) * mm, "end": v(-37.06, 127) * mm});
            skArc(sketch, "E24.49.0", {"start": v(-44.34, 136.48) * mm, "mid": v(-49.4, 134.73) * mm, "end": v(-54.38, 132.8) * mm});
            skLineSegment(sketch, "E24.49.1", {"start": v(-54.38, 132.8) * mm, "end": v(-50.13, 122.43) * mm});
            skLineSegment(sketch, "E24.49.2", {"start": v(-44.34, 136.48) * mm, "end": v(-40.88, 125.82) * mm});
            skArc(sketch, "E24.49.3", {"start": v(-40.88, 125.82) * mm, "mid": v(-45.54, 124.22) * mm, "end": v(-50.13, 122.43) * mm});
            skArc(sketch, "E24.50.0", {"start": v(-58.37, 131.1) * mm, "mid": v(-63.2, 128.83) * mm, "end": v(-67.96, 126.39) * mm});
            skLineSegment(sketch, "E24.50.1", {"start": v(-67.96, 126.39) * mm, "end": v(-62.66, 116.52) * mm});
            skLineSegment(sketch, "E24.50.2", {"start": v(-58.37, 131.1) * mm, "end": v(-53.81, 120.86) * mm});
            skArc(sketch, "E24.50.3", {"start": v(-53.81, 120.86) * mm, "mid": v(-58.27, 118.77) * mm, "end": v(-62.66, 116.52) * mm});
            skArc(sketch, "E24.51.0", {"start": v(-71.75, 124.27) * mm, "mid": v(-76.33, 121.52) * mm, "end": v(-80.8, 118.59) * mm});
            skLineSegment(sketch, "E24.51.1", {"start": v(-80.8, 118.59) * mm, "end": v(-74.5, 109.33) * mm});
            skLineSegment(sketch, "E24.51.2", {"start": v(-71.75, 124.27) * mm, "end": v(-66.15, 114.58) * mm});
            skArc(sketch, "E24.51.3", {"start": v(-66.15, 114.58) * mm, "mid": v(-70.37, 112.03) * mm, "end": v(-74.5, 109.33) * mm});
            skArc(sketch, "E24.52.0", {"start": v(-84.35, 116.1) * mm, "mid": v(-88.61, 112.87) * mm, "end": v(-92.75, 109.5) * mm});
            skLineSegment(sketch, "E24.52.1", {"start": v(-92.75, 109.5) * mm, "end": v(-85.51, 100.95) * mm});
            skLineSegment(sketch, "E24.52.2", {"start": v(-84.35, 116.1) * mm, "end": v(-77.76, 107.03) * mm});
            skArc(sketch, "E24.52.3", {"start": v(-77.76, 107.03) * mm, "mid": v(-81.7, 104.06) * mm, "end": v(-85.51, 100.95) * mm});
            skArc(sketch, "E24.53.0", {"start": v(-96.02, 106.64) * mm, "mid": v(-99.92, 103) * mm, "end": v(-103.7, 99.2) * mm});
            skLineSegment(sketch, "E24.53.1", {"start": v(-103.7, 99.2) * mm, "end": v(-95.6, 91.46) * mm});
            skLineSegment(sketch, "E24.53.2", {"start": v(-96.02, 106.64) * mm, "end": v(-88.53, 98.32) * mm});
            skArc(sketch, "E24.53.3", {"start": v(-88.53, 98.32) * mm, "mid": v(-92.13, 94.95) * mm, "end": v(-95.6, 91.46) * mm});
            skArc(sketch, "E24.54.0", {"start": v(-106.64, 96.02) * mm, "mid": v(-110.14, 91.98) * mm, "end": v(-113.5, 87.82) * mm});
            skLineSegment(sketch, "E24.54.1", {"start": v(-113.5, 87.82) * mm, "end": v(-104.63, 80.96) * mm});
            skLineSegment(sketch, "E24.54.2", {"start": v(-106.64, 96.02) * mm, "end": v(-98.32, 88.53) * mm});
            skArc(sketch, "E24.54.3", {"start": v(-98.32, 88.53) * mm, "mid": v(-101.55, 84.8) * mm, "end": v(-104.63, 80.96) * mm});
            skArc(sketch, "E24.55.0", {"start": v(-116.1, 84.35) * mm, "mid": v(-119.15, 79.97) * mm, "end": v(-122.05, 75.47) * mm});
            skLineSegment(sketch, "E24.55.1", {"start": v(-122.05, 75.47) * mm, "end": v(-112.52, 69.58) * mm});
            skLineSegment(sketch, "E24.55.2", {"start": v(-116.1, 84.35) * mm, "end": v(-107.03, 77.76) * mm});
            skArc(sketch, "E24.55.3", {"start": v(-107.03, 77.76) * mm, "mid": v(-109.85, 73.72) * mm, "end": v(-112.52, 69.58) * mm});
            skArc(sketch, "E24.56.0", {"start": v(-124.27, 71.75) * mm, "mid": v(-126.86, 67.07) * mm, "end": v(-129.27, 62.3) * mm});
            skLineSegment(sketch, "E24.56.1", {"start": v(-129.27, 62.3) * mm, "end": v(-119.18, 57.44) * mm});
            skLineSegment(sketch, "E24.56.2", {"start": v(-124.27, 71.75) * mm, "end": v(-114.58, 66.15) * mm});
            skArc(sketch, "E24.56.3", {"start": v(-114.58, 66.15) * mm, "mid": v(-116.96, 61.84) * mm, "end": v(-119.18, 57.44) * mm});
            skArc(sketch, "E24.57.0", {"start": v(-131.1, 58.37) * mm, "mid": v(-133.18, 53.44) * mm, "end": v(-135.07, 48.45) * mm});
            skLineSegment(sketch, "E24.57.1", {"start": v(-135.07, 48.45) * mm, "end": v(-124.53, 44.67) * mm});
            skLineSegment(sketch, "E24.57.2", {"start": v(-131.1, 58.37) * mm, "end": v(-120.86, 53.81) * mm});
            skArc(sketch, "E24.57.3", {"start": v(-120.86, 53.81) * mm, "mid": v(-122.78, 49.27) * mm, "end": v(-124.53, 44.67) * mm});
            skArc(sketch, "E24.58.0", {"start": v(-136.48, 44.34) * mm, "mid": v(-138.03, 39.23) * mm, "end": v(-139.4, 34.06) * mm});
            skLineSegment(sketch, "E24.58.1", {"start": v(-139.4, 34.06) * mm, "end": v(-128.52, 31.4) * mm});
            skLineSegment(sketch, "E24.58.2", {"start": v(-136.48, 44.34) * mm, "end": v(-125.82, 40.88) * mm});
            skArc(sketch, "E24.58.3", {"start": v(-125.82, 40.88) * mm, "mid": v(-127.26, 36.17) * mm, "end": v(-128.52, 31.4) * mm});
            skArc(sketch, "E24.59.0", {"start": v(-140.36, 29.84) * mm, "mid": v(-141.38, 24.59) * mm, "end": v(-142.2, 19.3) * mm});
            skLineSegment(sketch, "E24.59.1", {"start": v(-142.2, 19.3) * mm, "end": v(-131.1, 17.8) * mm});
            skLineSegment(sketch, "E24.59.2", {"start": v(-140.36, 29.84) * mm, "end": v(-129.4, 27.5) * mm});
            skArc(sketch, "E24.59.3", {"start": v(-129.4, 27.5) * mm, "mid": v(-130.34, 22.67) * mm, "end": v(-131.1, 17.8) * mm});
            skSolve(sketch);
        }
        {
            var Q0;
            Q0 = qSketchRegion(id + "F4", true);
            extrude(context, id + "F5", {"entities" : qUnion([Q0]), "operationType" : NewBodyOperationType.REMOVE, "depth" : 14.6 * mm});
        }
    });
